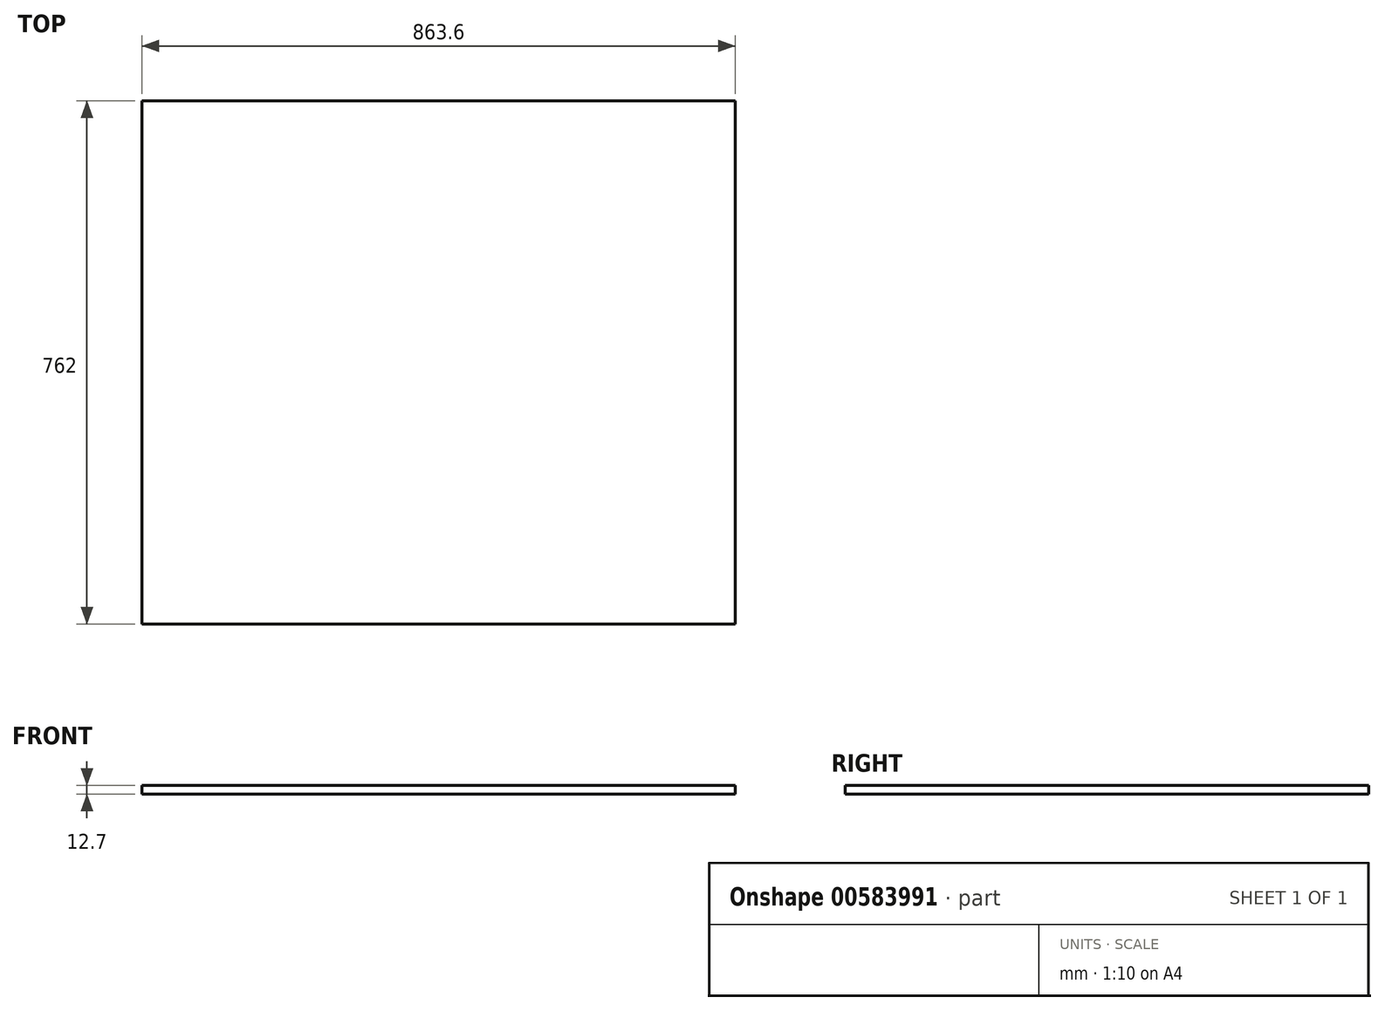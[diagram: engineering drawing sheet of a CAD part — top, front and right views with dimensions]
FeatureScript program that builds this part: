
annotation { "Feature Type Name" : "Feature", "Feature Type Description" : "" }
export const myFeature = defineFeature(function(context is Context, id is Id, definition is map)
    precondition{}
    {
        {
            var Q0;
            Q0=qCreatedBy(makeId("Top.planeOp"),FACE);
            var sketch = newSketch(context, id + "F0", { "sketchPlane" : qUnion([Q0])});
            skLineSegment(sketch, "E0.bottom", {"start": v(-472.4, 396.37) * mm, "end": v(391.2, 396.37) * mm});
            skLineSegment(sketch, "E0.top", {"start": v(-472.4, -365.63) * mm, "end": v(391.2, -365.63) * mm});
            skLineSegment(sketch, "E0.left", {"start": v(-472.4, 396.37) * mm, "end": v(-472.4, -365.63) * mm});
            skLineSegment(sketch, "E0.right", {"start": v(391.2, 396.37) * mm, "end": v(391.2, -365.63) * mm});
            skSolve(sketch);
        }
        {
            var Q0;
            Q0 = qSketchRegion(id + "F0", true);
            extrude(context, id + "F1", {"entities" : qUnion([Q0]), "depth" : 12.7 * mm, "offsetDistance" : 25.4 * mm});
        }
    });
